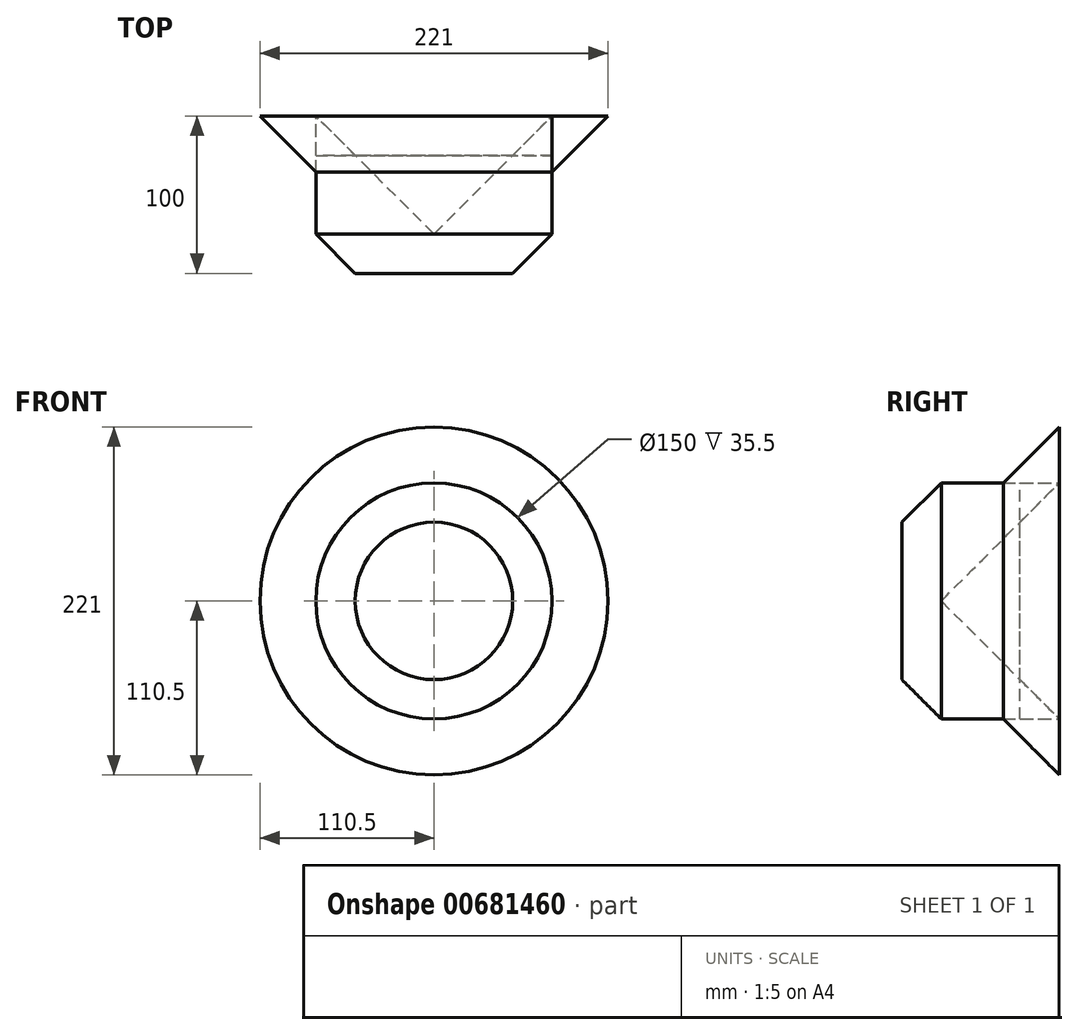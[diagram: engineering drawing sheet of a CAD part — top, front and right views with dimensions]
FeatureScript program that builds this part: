
annotation { "Feature Type Name" : "Feature", "Feature Type Description" : "" }
export const myFeature = defineFeature(function(context is Context, id is Id, definition is map)
    precondition{}
    {
        {
            var Q0;
            Q0=qCreatedBy(makeId("Front.planeOp"),FACE);
            var sketch = newSketch(context, id + "F0", { "sketchPlane" : qUnion([Q0])});
            skCircle(sketch, "E0", {"center": v(0, 0) * mm, "radius": 75 * mm});
            skSolve(sketch);
        }
        {
            var Q0;
            Q0=makeQuery(id+"F0.imprint","IMPRINT",FACE,{"disambiguationData":[TD([[makeQuery(id+"F0.imprint","IMPRINT",EDGE,{"derivedFrom":sQuery(id+"F0.wireOp",EDGE,"E0")}),1.0]])]});
            extrude(context, id + "F1", {"entities" : qUnion([Q0]), "depth" : 100 * mm, "offsetDistance" : 25 * mm});
        }
        {
            var Q0;
            Q0=makeQuery(id+"F1.opExtrude","CAP_EDGE",EDGE,{"disambiguationData":[OSD([sQuery(id+"F0.wireOp",EDGE,"E0")])],"isStart":false});
            chamfer(context, id + "F2", {"entities" : qUnion([Q0]), "width" : 25 * mm, "tangentPropagation" : true});
        }
        {
            var Q0;
            Q0=qCreatedBy(makeId("Front.planeOp"),FACE);
            var sketch = newSketch(context, id + "F3", { "sketchPlane" : qUnion([Q0])});
            skCircle(sketch, "E1", {"center": v(0, 0) * mm, "radius": 50 * mm});
            skCircle(sketch, "E2", {"center": v(0, 0) * mm, "radius": 75 * mm});
            skSolve(sketch);
        }
        {
            var Q0;
            Q0=makeQuery(id+"F3.imprint","IMPRINT",FACE,{"disambiguationData":[TD([[makeQuery(id+"F3.imprint","IMPRINT",EDGE,{"derivedFrom":sQuery(id+"F3.wireOp",EDGE,"E1")}),-1.0]])]});
            extrude(context, id + "F4", {"entities" : qUnion([Q0]), "depth" : 25 * mm, "offsetDistance" : 25 * mm});
        }
        {
            var Q0;
            Q0=makeQuery(id+"F4.opExtrude","CAP_EDGE",EDGE,{"disambiguationData":[OSD([sQuery(id+"F3.wireOp",EDGE,"E1")])],"isStart":true});
            chamfer(context, id + "F5", {"entities" : qUnion([Q0]), "width" : 25 * mm, "tangentPropagation" : true});
        }
        {
            var Q0;
            Q0=qCreatedBy(makeId("Front.planeOp"),FACE);
            var sketch = newSketch(context, id + "F6", { "sketchPlane" : qUnion([Q0])});
            skCircle(sketch, "E3", {"center": v(0, 0) * mm, "radius": 75 * mm});
            skCircle(sketch, "E4", {"center": v(0, 0) * mm, "radius": 110.5 * mm});
            skSolve(sketch);
        }
        {
            var Q0;
            Q0=makeQuery(id+"F6.imprint","IMPRINT",FACE,{"disambiguationData":[TD([[makeQuery(id+"F6.imprint","IMPRINT",EDGE,{"derivedFrom":sQuery(id+"F6.wireOp",EDGE,"E3")}),-1.0]])]});
            extrude(context, id + "F7", {"entities" : qUnion([Q0]), "depth" : 35.5 * mm, "offsetDistance" : 25 * mm});
        }
        {
            var Q0;
            Q0=makeQuery(id+"F7.opExtrude","CAP_EDGE",EDGE,{"disambiguationData":[OSD([sQuery(id+"F6.wireOp",EDGE,"E4")])],"isStart":false});
            chamfer(context, id + "F8", {"entities" : qUnion([Q0]), "width" : 35.5 * mm, "tangentPropagation" : true});
        }
        {
            var Q0;
            Q0=makeQuery(id+"F7.opExtrude","SWEPT_BODY",BODY,{"disambiguationData":[OSD([sQuery(id+"F6.wireOp",EDGE,"E3"),sQuery(id+"F6.wireOp",EDGE,"E4")])]});
            transform(context, id + "F9", {"entities" : qUnion([Q0]), "transformType" : TransformType.TRANSLATION_3D, "dx" : 0 * mm, "dy" : 0 * mm, "dz" : 0 * mm, "makeCopy" : true});
        }
        {
            var Q0;
            Q0=makeQuery(id+"F9.opPattern","COPY",BODY,{"derivedFrom":makeQuery(id+"F7.opExtrude","SWEPT_BODY",BODY,{"disambiguationData":[OSD([sQuery(id+"F6.wireOp",EDGE,"E3"),sQuery(id+"F6.wireOp",EDGE,"E4")])]}),"instanceName":"1"});
            deleteBodies(context, id + "F10", {"entities" : qUnion([Q0])});
        }
        {
            var Q0;
            Q0=qCreatedBy(makeId("Front.planeOp"),FACE);
            var sketch = newSketch(context, id + "F11", { "sketchPlane" : qUnion([Q0])});
            skCircle(sketch, "E5", {"center": v(0, 0) * mm, "radius": 75 * mm});
            skSolve(sketch);
        }
        {
            var Q0;
            Q0=makeQuery(id+"F11.imprint","IMPRINT",FACE,{"disambiguationData":[TD([[makeQuery(id+"F11.imprint","IMPRINT",EDGE,{"derivedFrom":sQuery(id+"F11.wireOp",EDGE,"E5")}),1.0]])]});
            extrude(context, id + "F12", {"entities" : qUnion([Q0]), "depth" : 75 * mm, "offsetDistance" : 25 * mm});
        }
        {
            var Q0;
            Q0=makeQuery(id+"F12.opExtrude","CAP_EDGE",EDGE,{"disambiguationData":[OSD([sQuery(id+"F11.wireOp",EDGE,"E5")])],"isStart":false});
            chamfer(context, id + "F13", {"entities" : qUnion([Q0]), "width" : 75 * mm, "tangentPropagation" : true});
        }
    });
